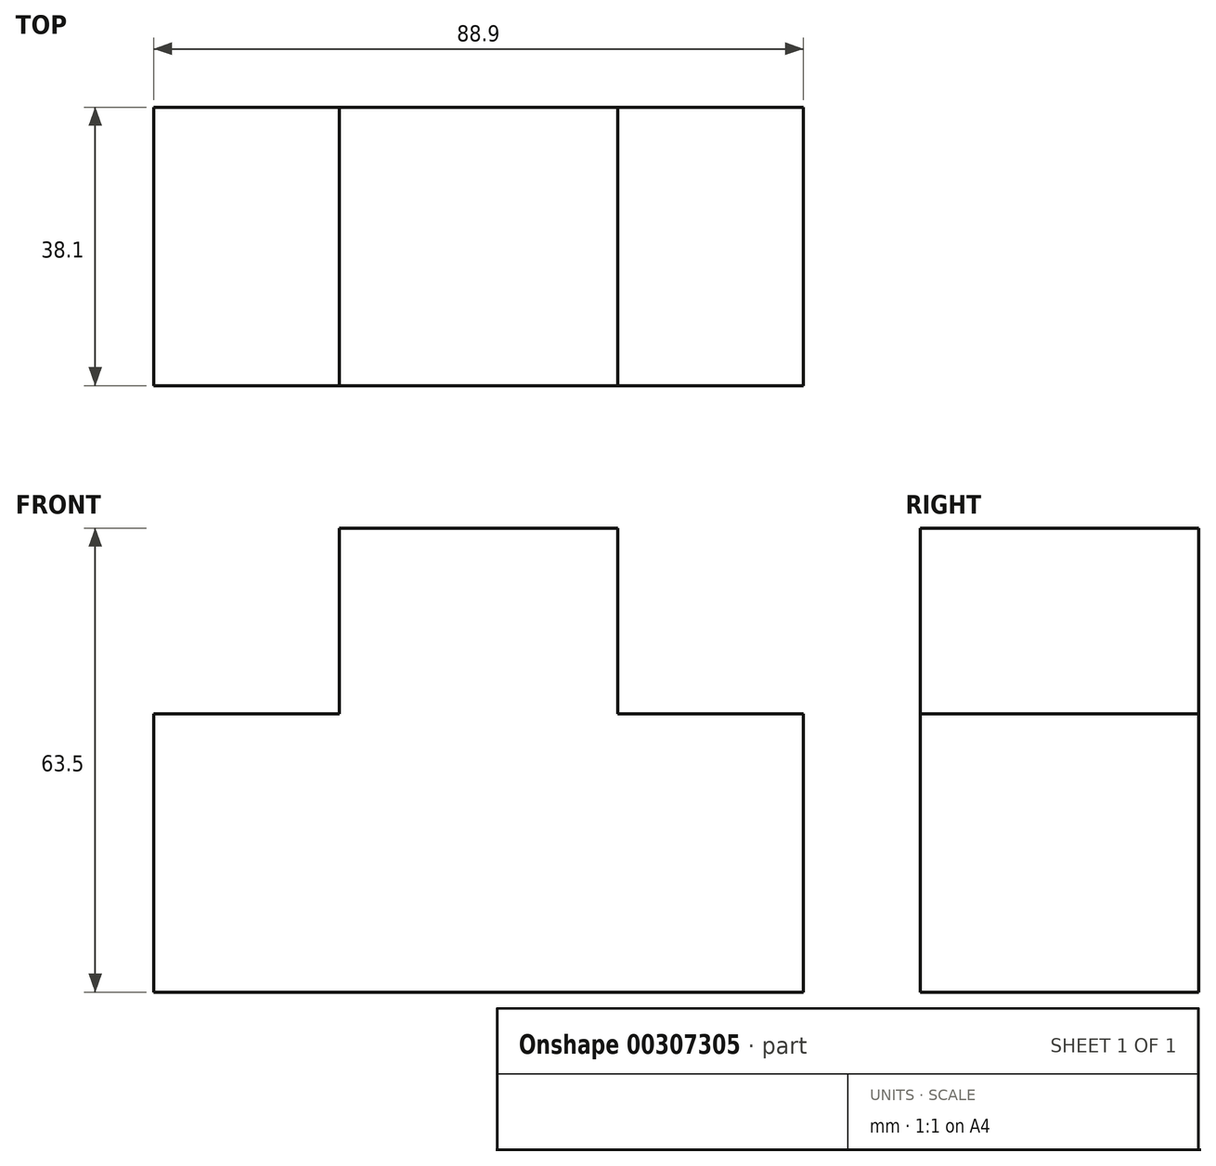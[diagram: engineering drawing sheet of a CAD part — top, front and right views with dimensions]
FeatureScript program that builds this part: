
annotation { "Feature Type Name" : "Feature", "Feature Type Description" : "" }
export const myFeature = defineFeature(function(context is Context, id is Id, definition is map)
    precondition{}
    {
        {
            var Q0;
            Q0=qCreatedBy(makeId("Front.planeOp"),FACE);
            var sketch = newSketch(context, id + "F0", { "sketchPlane" : qUnion([Q0])});
            skLineSegment(sketch, "E0", {"start": v(36.9, -40.75) * mm, "end": v(36.9, -2.65) * mm});
            skLineSegment(sketch, "E1", {"start": v(36.9, -2.65) * mm, "end": v(11.5, -2.65) * mm});
            skLineSegment(sketch, "E2", {"start": v(11.5, -2.65) * mm, "end": v(11.5, 22.75) * mm});
            skLineSegment(sketch, "E3", {"start": v(11.5, 22.75) * mm, "end": v(-26.6, 22.75) * mm});
            skLineSegment(sketch, "E4", {"start": v(-26.6, 22.75) * mm, "end": v(-26.6, -2.65) * mm});
            skLineSegment(sketch, "E5", {"start": v(-26.6, -2.65) * mm, "end": v(-52, -2.65) * mm});
            skLineSegment(sketch, "E6", {"start": v(-52, -2.65) * mm, "end": v(-52, -40.75) * mm});
            skLineSegment(sketch, "E7", {"start": v(-52, -40.75) * mm, "end": v(36.9, -40.75) * mm});
            skSolve(sketch);
        }
        {
            var Q0;
            Q0=makeQuery(id+"F0.imprint","IMPRINT",FACE,{"disambiguationData":[TD([[makeQuery(id+"F0.imprint","IMPRINT",EDGE,{"derivedFrom":sQuery(id+"F0.wireOp",EDGE,"E0")}),1.0]])]});
            extrude(context, id + "F1", {"entities" : qUnion([Q0]), "depth" : 38.1 * mm});
        }
    });
